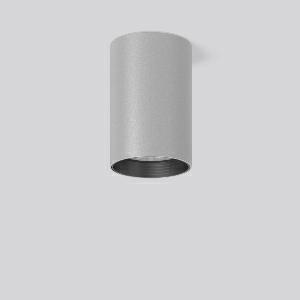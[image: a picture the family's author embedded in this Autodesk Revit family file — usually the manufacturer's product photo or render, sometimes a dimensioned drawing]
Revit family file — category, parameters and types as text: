
# Revit family: heledon_maxi_a_931229_004_2_76_0394
name_source: partatom
category: Lighting Fixtures
units: mm (PartAtom-declared; Revit-internal decimal feet)

## family parameters
Cut with Voids When Loaded = No
Host = Face
Light Source = No
Part Type = Normal
Room Calculation Point = No
Round Connector Dimension = Use Diameter
Shared = No

## types (1)
- HELEDON maxi A (1 x LED Modul 927, 3450 lm, 2700)
    Apparent Load = 35 VA
    Approval mark = CE
    CIE Flux Codes = 96 100 100 100 100
    Color Rendering = 92
    Color Temperature = 2700
    Default Elevation = 1800 mm
    Description = Series: HELEDON maxi
Cylindrical surface-mounted downlight. Housing: die-cast aluminium, powder-coated. Internal ceiling frame polycarbonate with bayonet mounting. Black plastic ring and recessed LED to prevent glare from the side. Optical assembly with lens made of plastic (polycarbonate) for the best homogeneous light distribution - can be changed without tools. Best colour rendering index Ra>90. Suitable for Ceiling mounting. Easy installation with a separate ceiling frame with bayonet mounting and plug connection. Driver integrated. Connected via plug-in connector. High quality converter without flickering and stroboscopic effect. The following accessories can be mounted without use of tools: interchangeable lenses, decorative glasses, honeycomb louvre, clear and frosted diffusers, white interchangeable plastic ring. 
Colour: silver
Diameter: 123 mm
Height: 183 mm
Lamp: LED
Socket: without socket
Colour temperature: 2700K
Colour rendering index (CRI): 92
System power: 35 W
Rated luminous flux: 3450 lm
Luminous efficiency: 99 lm/W
Control gear: Converter, dimmable, DALI
Protection class: I
Type of protection: IP 20
    Height = 183 mm
    Lamp = 1 x LED Modul 927
    Lamp Light Flux = 3450 lm
    Lamp count = 1
    Length = 123 mm
    Lifetime = 50000 h
    Luminous efficacy = 99 lm/W
    Manufacturer = RZB
    ModVariant = No
    Model = 931229.004.2.76
    Mounting Place = Ceiling
    Mounting Type = Surface mounted
    Number of Poles = 1
    OnlyDefault = Yes
    Power Factor = 1
    Product Name = HELEDON maxi A
    Product group = Surface mounted downlights
    ProductGroupID = 302
    Protection Class = Protection class I
    Protection Degree = IP 20
    RLX_Detail_Level = 1
    RLX_Emergency_Light_Flux = 0 lm
    RLX_Emergency_Type = 0
    RLX_Emergency_Type_DB = No
    RlxData = <blob elided: 98301 chars, md5=1489063f>
    Socket = socket
    Standby Power = 0 W
    System Light Flux = 3450 lm
    System Power = 35 W
    Type Comments = Product without accessories
    Type Image = 931193.004.jpg
    URL = http://relux.com
    VarID = ---
    Voltage = 230 V
    Voltage Range = 220-240 V
    Weight = 0.00 kg
    Width = 0 mm  [stored 0 ft]

note: [stored X ft] marks values corroborated as IEEE doubles in the binary element streams (Revit-internal decimal feet)

## geometry (parser evidence)
native form markers: Blend x4, Sweep x9
no freeform markers — native parametric forms only
